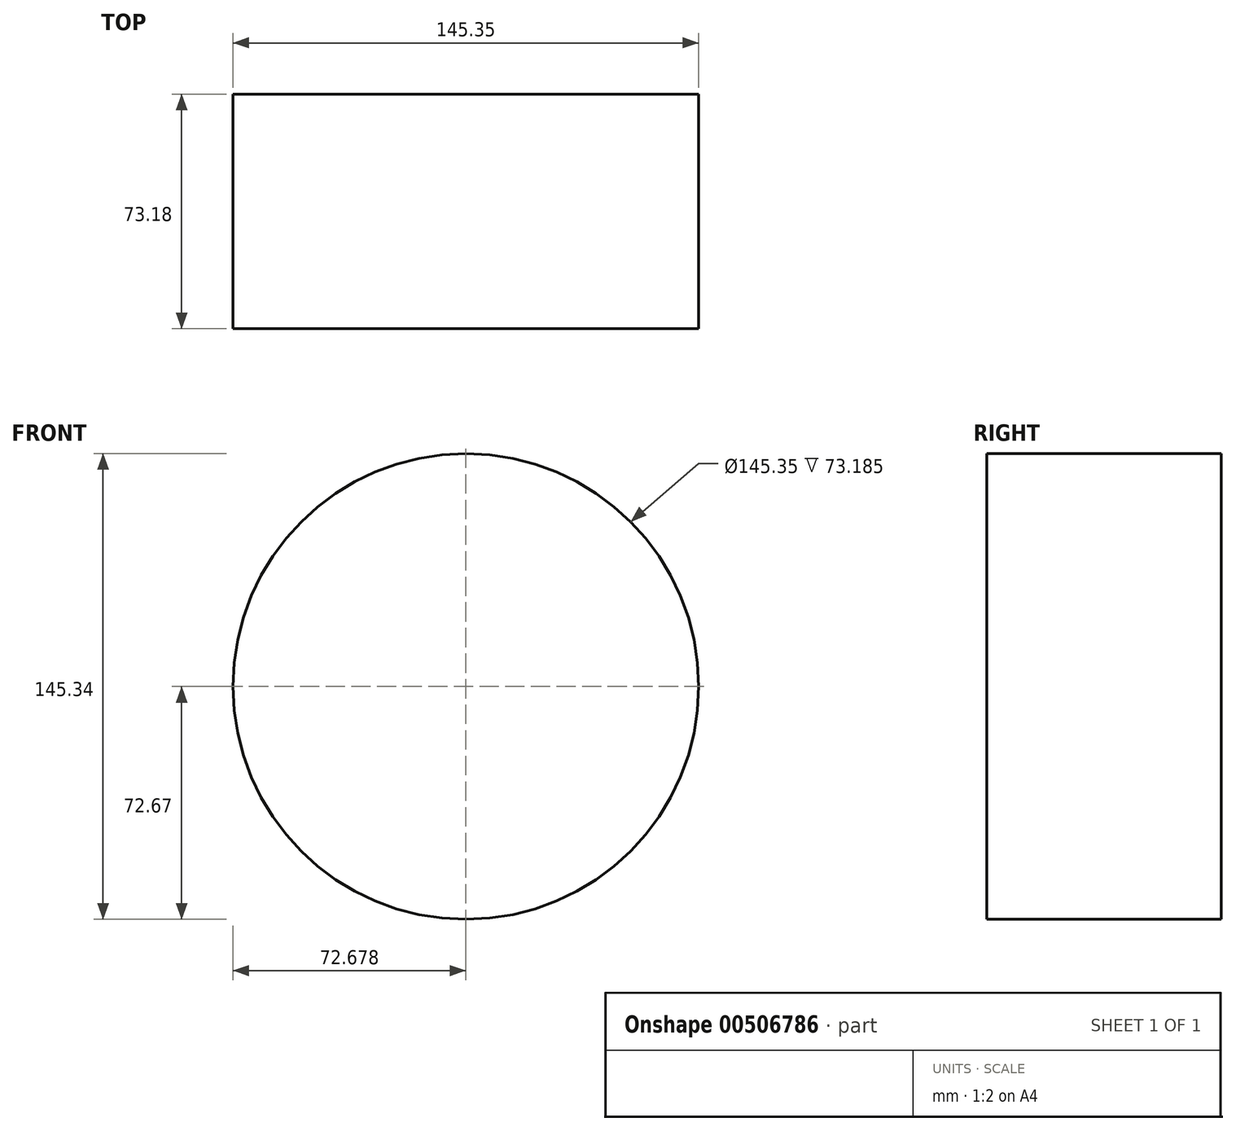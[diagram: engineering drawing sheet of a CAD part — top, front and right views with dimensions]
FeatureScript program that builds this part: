
annotation { "Feature Type Name" : "Feature", "Feature Type Description" : "" }
export const myFeature = defineFeature(function(context is Context, id is Id, definition is map)
    precondition{}
    {
        {
            var Q0;
            Q0=qCreatedBy(makeId("Top.planeOp"),FACE);
            var sketch = newSketch(context, id + "F0", { "sketchPlane" : qUnion([Q0])});
            skLineSegment(sketch, "E0.bottom", {"start": v(-111.4, 43.95) * mm, "end": v(-38.73, 43.95) * mm});
            skLineSegment(sketch, "E0.top", {"start": v(-111.4, -29.23) * mm, "end": v(-38.73, -29.23) * mm});
            skLineSegment(sketch, "E0.left", {"start": v(-111.4, 43.95) * mm, "end": v(-111.4, -29.23) * mm});
            skLineSegment(sketch, "E0.right", {"start": v(-38.73, 43.95) * mm, "end": v(-38.73, -29.23) * mm, "construction": true});
            skSolve(sketch);
        }
        {
            var Q0;
            Q0=sQuery(id+"F0.wireOp",EDGE,"E0.top");
            var Q1;
            Q1=sQuery(id+"F0.wireOp",EDGE,"E0.left");
            var Q2;
            Q2=sQuery(id+"F0.wireOp",EDGE,"E0.bottom");
            var Q3;
            Q3=sQuery(id+"F0.wireOp",EDGE,"E0.right");
            revolve(context, id + "F1", {"bodyType" : ToolBodyType.SURFACE, "surfaceEntities" : qUnion([Q0, Q1, Q2]), "axis" : qUnion([Q3]), "revolveType" : RevolveType.FULL});
        }
    });
